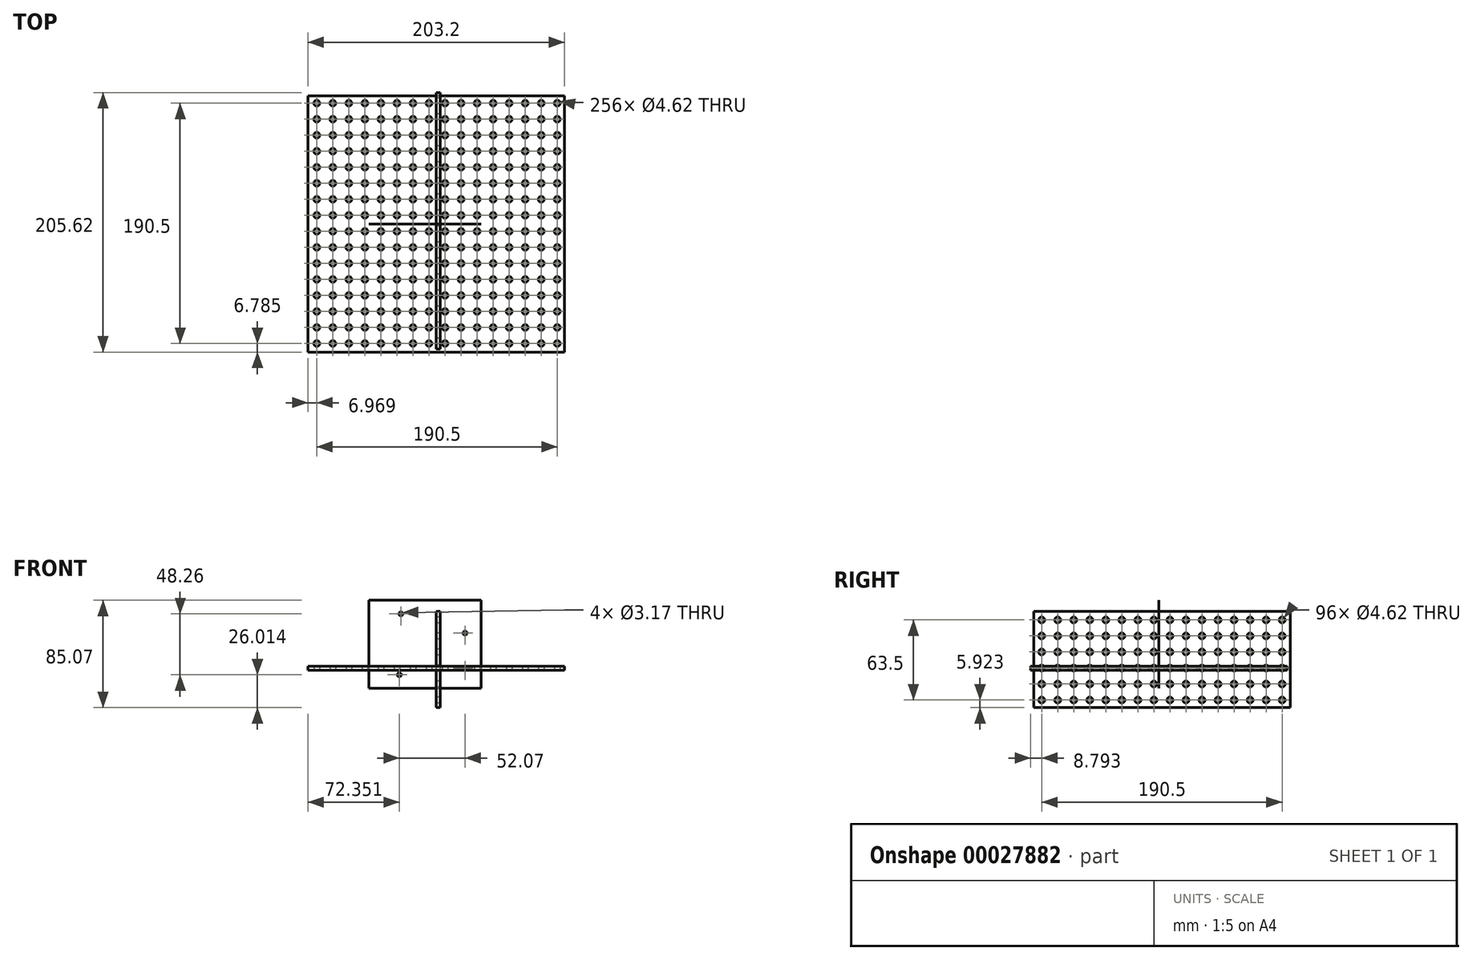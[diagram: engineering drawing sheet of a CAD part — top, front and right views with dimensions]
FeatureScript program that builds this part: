
annotation { "Feature Type Name" : "Feature", "Feature Type Description" : "" }
export const myFeature = defineFeature(function(context is Context, id is Id, definition is map)
    precondition{}
    {
        {
            var Q0;
            Q0=qCreatedBy(makeId("Top.planeOp"),FACE);
            var sketch = newSketch(context, id + "F0", { "sketchPlane" : qUnion([Q0])});
            skLineSegment(sketch, "E0.rect.bottom", {"start": v(101.6, 101.6) * mm, "end": v(-101.6, 101.6) * mm});
            skLineSegment(sketch, "E0.rect.left", {"start": v(101.6, 101.6) * mm, "end": v(101.6, -101.6) * mm});
            skLineSegment(sketch, "E0.rect.right", {"start": v(-101.6, 101.6) * mm, "end": v(-101.6, -101.6) * mm});
            skPoint(sketch, "E0.rect.middle", {"position": v(0, 0) * mm});
            skCircle(sketch, "E1", {"center": v(-94.63, 95.69) * mm, "radius": 2.31 * mm});
            skCircle(sketch, "E2.0.1.0", {"center": v(-94.63, 82.99) * mm, "radius": 2.31 * mm});
            skCircle(sketch, "E2.0.2.0", {"center": v(-94.63, 70.29) * mm, "radius": 2.31 * mm});
            skCircle(sketch, "E2.0.3.0", {"center": v(-94.63, 57.59) * mm, "radius": 2.31 * mm});
            skCircle(sketch, "E2.0.4.0", {"center": v(-94.63, 44.89) * mm, "radius": 2.31 * mm});
            skCircle(sketch, "E2.0.5.0", {"center": v(-94.63, 32.19) * mm, "radius": 2.31 * mm});
            skCircle(sketch, "E2.0.6.0", {"center": v(-94.63, 19.49) * mm, "radius": 2.31 * mm});
            skCircle(sketch, "E2.0.7.0", {"center": v(-94.63, 6.79) * mm, "radius": 2.31 * mm});
            skCircle(sketch, "E2.0.8.0", {"center": v(-94.63, -5.91) * mm, "radius": 2.31 * mm});
            skCircle(sketch, "E2.0.9.0", {"center": v(-94.63, -18.61) * mm, "radius": 2.31 * mm});
            skCircle(sketch, "E2.1.0.0", {"center": v(-81.93, 95.69) * mm, "radius": 2.31 * mm});
            skCircle(sketch, "E2.1.1.0", {"center": v(-81.93, 82.99) * mm, "radius": 2.31 * mm});
            skCircle(sketch, "E2.1.2.0", {"center": v(-81.93, 70.29) * mm, "radius": 2.31 * mm});
            skCircle(sketch, "E2.1.3.0", {"center": v(-81.93, 57.59) * mm, "radius": 2.31 * mm});
            skCircle(sketch, "E2.1.4.0", {"center": v(-81.93, 44.89) * mm, "radius": 2.31 * mm});
            skCircle(sketch, "E2.1.5.0", {"center": v(-81.93, 32.19) * mm, "radius": 2.31 * mm});
            skCircle(sketch, "E2.1.6.0", {"center": v(-81.93, 19.49) * mm, "radius": 2.31 * mm});
            skCircle(sketch, "E2.1.7.0", {"center": v(-81.93, 6.79) * mm, "radius": 2.31 * mm});
            skCircle(sketch, "E2.1.8.0", {"center": v(-81.93, -5.91) * mm, "radius": 2.31 * mm});
            skCircle(sketch, "E2.1.9.0", {"center": v(-81.93, -18.61) * mm, "radius": 2.31 * mm});
            skCircle(sketch, "E2.2.0.0", {"center": v(-69.23, 95.69) * mm, "radius": 2.31 * mm});
            skCircle(sketch, "E2.2.1.0", {"center": v(-69.23, 82.99) * mm, "radius": 2.31 * mm});
            skCircle(sketch, "E2.2.2.0", {"center": v(-69.23, 70.29) * mm, "radius": 2.31 * mm});
            skCircle(sketch, "E2.2.3.0", {"center": v(-69.23, 57.59) * mm, "radius": 2.31 * mm});
            skCircle(sketch, "E2.2.4.0", {"center": v(-69.23, 44.89) * mm, "radius": 2.31 * mm});
            skCircle(sketch, "E2.2.5.0", {"center": v(-69.23, 32.19) * mm, "radius": 2.31 * mm});
            skCircle(sketch, "E2.2.6.0", {"center": v(-69.23, 19.49) * mm, "radius": 2.31 * mm});
            skCircle(sketch, "E2.2.7.0", {"center": v(-69.23, 6.79) * mm, "radius": 2.31 * mm});
            skCircle(sketch, "E2.2.8.0", {"center": v(-69.23, -5.91) * mm, "radius": 2.31 * mm});
            skCircle(sketch, "E2.2.9.0", {"center": v(-69.23, -18.61) * mm, "radius": 2.31 * mm});
            skCircle(sketch, "E2.3.0.0", {"center": v(-56.53, 95.69) * mm, "radius": 2.31 * mm});
            skCircle(sketch, "E2.3.1.0", {"center": v(-56.53, 82.99) * mm, "radius": 2.31 * mm});
            skCircle(sketch, "E2.3.2.0", {"center": v(-56.53, 70.29) * mm, "radius": 2.31 * mm});
            skCircle(sketch, "E2.3.3.0", {"center": v(-56.53, 57.59) * mm, "radius": 2.31 * mm});
            skCircle(sketch, "E2.3.4.0", {"center": v(-56.53, 44.89) * mm, "radius": 2.31 * mm});
            skCircle(sketch, "E2.3.5.0", {"center": v(-56.53, 32.19) * mm, "radius": 2.31 * mm});
            skCircle(sketch, "E2.3.6.0", {"center": v(-56.53, 19.49) * mm, "radius": 2.31 * mm});
            skCircle(sketch, "E2.3.7.0", {"center": v(-56.53, 6.79) * mm, "radius": 2.31 * mm});
            skCircle(sketch, "E2.3.8.0", {"center": v(-56.53, -5.91) * mm, "radius": 2.31 * mm});
            skCircle(sketch, "E2.3.9.0", {"center": v(-56.53, -18.61) * mm, "radius": 2.31 * mm});
            skCircle(sketch, "E2.4.0.0", {"center": v(-43.83, 95.69) * mm, "radius": 2.31 * mm});
            skCircle(sketch, "E2.4.1.0", {"center": v(-43.83, 82.99) * mm, "radius": 2.31 * mm});
            skCircle(sketch, "E2.4.2.0", {"center": v(-43.83, 70.29) * mm, "radius": 2.31 * mm});
            skCircle(sketch, "E2.4.3.0", {"center": v(-43.83, 57.59) * mm, "radius": 2.31 * mm});
            skCircle(sketch, "E2.4.4.0", {"center": v(-43.83, 44.89) * mm, "radius": 2.31 * mm});
            skCircle(sketch, "E2.4.5.0", {"center": v(-43.83, 32.19) * mm, "radius": 2.31 * mm});
            skCircle(sketch, "E2.4.6.0", {"center": v(-43.83, 19.49) * mm, "radius": 2.31 * mm});
            skCircle(sketch, "E2.4.7.0", {"center": v(-43.83, 6.79) * mm, "radius": 2.31 * mm});
            skCircle(sketch, "E2.4.8.0", {"center": v(-43.83, -5.91) * mm, "radius": 2.31 * mm});
            skCircle(sketch, "E2.4.9.0", {"center": v(-43.83, -18.61) * mm, "radius": 2.31 * mm});
            skCircle(sketch, "E2.5.0.0", {"center": v(-31.13, 95.69) * mm, "radius": 2.31 * mm});
            skCircle(sketch, "E2.5.1.0", {"center": v(-31.13, 82.99) * mm, "radius": 2.31 * mm});
            skCircle(sketch, "E2.5.2.0", {"center": v(-31.13, 70.29) * mm, "radius": 2.31 * mm});
            skCircle(sketch, "E2.5.3.0", {"center": v(-31.13, 57.59) * mm, "radius": 2.31 * mm});
            skCircle(sketch, "E2.5.4.0", {"center": v(-31.13, 44.89) * mm, "radius": 2.31 * mm});
            skCircle(sketch, "E2.5.5.0", {"center": v(-31.13, 32.19) * mm, "radius": 2.31 * mm});
            skCircle(sketch, "E2.5.6.0", {"center": v(-31.13, 19.49) * mm, "radius": 2.31 * mm});
            skCircle(sketch, "E2.5.7.0", {"center": v(-31.13, 6.79) * mm, "radius": 2.31 * mm});
            skCircle(sketch, "E2.5.8.0", {"center": v(-31.13, -5.91) * mm, "radius": 2.31 * mm});
            skCircle(sketch, "E2.5.9.0", {"center": v(-31.13, -18.61) * mm, "radius": 2.31 * mm});
            skCircle(sketch, "E2.6.0.0", {"center": v(-18.43, 95.69) * mm, "radius": 2.31 * mm});
            skCircle(sketch, "E2.6.1.0", {"center": v(-18.43, 82.99) * mm, "radius": 2.31 * mm});
            skCircle(sketch, "E2.6.2.0", {"center": v(-18.43, 70.29) * mm, "radius": 2.31 * mm});
            skCircle(sketch, "E2.6.3.0", {"center": v(-18.43, 57.59) * mm, "radius": 2.31 * mm});
            skCircle(sketch, "E2.6.4.0", {"center": v(-18.43, 44.89) * mm, "radius": 2.31 * mm});
            skCircle(sketch, "E2.6.5.0", {"center": v(-18.43, 32.19) * mm, "radius": 2.31 * mm});
            skCircle(sketch, "E2.6.6.0", {"center": v(-18.43, 19.49) * mm, "radius": 2.31 * mm});
            skCircle(sketch, "E2.6.7.0", {"center": v(-18.43, 6.79) * mm, "radius": 2.31 * mm});
            skCircle(sketch, "E2.6.8.0", {"center": v(-18.43, -5.91) * mm, "radius": 2.31 * mm});
            skCircle(sketch, "E2.6.9.0", {"center": v(-18.43, -18.61) * mm, "radius": 2.31 * mm});
            skCircle(sketch, "E2.7.0.0", {"center": v(-5.73, 95.69) * mm, "radius": 2.31 * mm});
            skCircle(sketch, "E2.7.1.0", {"center": v(-5.73, 82.99) * mm, "radius": 2.31 * mm});
            skCircle(sketch, "E2.7.2.0", {"center": v(-5.73, 70.29) * mm, "radius": 2.31 * mm});
            skCircle(sketch, "E2.7.3.0", {"center": v(-5.73, 57.59) * mm, "radius": 2.31 * mm});
            skCircle(sketch, "E2.7.4.0", {"center": v(-5.73, 44.89) * mm, "radius": 2.31 * mm});
            skCircle(sketch, "E2.7.5.0", {"center": v(-5.73, 32.19) * mm, "radius": 2.31 * mm});
            skCircle(sketch, "E2.7.6.0", {"center": v(-5.73, 19.49) * mm, "radius": 2.31 * mm});
            skCircle(sketch, "E2.7.7.0", {"center": v(-5.73, 6.79) * mm, "radius": 2.31 * mm});
            skCircle(sketch, "E2.7.8.0", {"center": v(-5.73, -5.91) * mm, "radius": 2.31 * mm});
            skCircle(sketch, "E2.7.9.0", {"center": v(-5.73, -18.61) * mm, "radius": 2.31 * mm});
            skCircle(sketch, "E2.8.0.0", {"center": v(6.97, 95.69) * mm, "radius": 2.31 * mm});
            skCircle(sketch, "E2.8.1.0", {"center": v(6.97, 82.99) * mm, "radius": 2.31 * mm});
            skCircle(sketch, "E2.8.2.0", {"center": v(6.97, 70.29) * mm, "radius": 2.31 * mm});
            skCircle(sketch, "E2.8.3.0", {"center": v(6.97, 57.59) * mm, "radius": 2.31 * mm});
            skCircle(sketch, "E2.8.4.0", {"center": v(6.97, 44.89) * mm, "radius": 2.31 * mm});
            skCircle(sketch, "E2.8.5.0", {"center": v(6.97, 32.19) * mm, "radius": 2.31 * mm});
            skCircle(sketch, "E2.8.6.0", {"center": v(6.97, 19.49) * mm, "radius": 2.31 * mm});
            skCircle(sketch, "E2.8.7.0", {"center": v(6.97, 6.79) * mm, "radius": 2.31 * mm});
            skCircle(sketch, "E2.8.8.0", {"center": v(6.97, -5.91) * mm, "radius": 2.31 * mm});
            skCircle(sketch, "E2.8.9.0", {"center": v(6.97, -18.61) * mm, "radius": 2.31 * mm});
            skCircle(sketch, "E2.9.0.0", {"center": v(19.67, 95.69) * mm, "radius": 2.31 * mm});
            skCircle(sketch, "E2.9.1.0", {"center": v(19.67, 82.99) * mm, "radius": 2.31 * mm});
            skCircle(sketch, "E2.9.2.0", {"center": v(19.67, 70.29) * mm, "radius": 2.31 * mm});
            skCircle(sketch, "E2.9.3.0", {"center": v(19.67, 57.59) * mm, "radius": 2.31 * mm});
            skCircle(sketch, "E2.9.4.0", {"center": v(19.67, 44.89) * mm, "radius": 2.31 * mm});
            skCircle(sketch, "E2.9.5.0", {"center": v(19.67, 32.19) * mm, "radius": 2.31 * mm});
            skCircle(sketch, "E2.9.6.0", {"center": v(19.67, 19.49) * mm, "radius": 2.31 * mm});
            skCircle(sketch, "E2.9.7.0", {"center": v(19.67, 6.79) * mm, "radius": 2.31 * mm});
            skCircle(sketch, "E2.9.8.0", {"center": v(19.67, -5.91) * mm, "radius": 2.31 * mm});
            skCircle(sketch, "E2.9.9.0", {"center": v(19.67, -18.61) * mm, "radius": 2.31 * mm});
            skLineSegment(sketch, "E2.direction1", {"start": v(-94.63, 95.69) * mm, "end": v(-81.93, 95.69) * mm, "construction": true});
            skLineSegment(sketch, "E2.direction2", {"start": v(-94.63, 95.69) * mm, "end": v(-94.63, 82.99) * mm, "construction": true});
            skCircle(sketch, "E3.0.0.10", {"center": v(-94.63, -31.31) * mm, "radius": 2.31 * mm});
            skCircle(sketch, "E3.0.0.11", {"center": v(-94.63, -44.01) * mm, "radius": 2.31 * mm});
            skCircle(sketch, "E3.0.0.12", {"center": v(-94.63, -56.71) * mm, "radius": 2.31 * mm});
            skCircle(sketch, "E3.0.0.13", {"center": v(-94.63, -69.41) * mm, "radius": 2.31 * mm});
            skCircle(sketch, "E3.0.0.14", {"center": v(-94.63, -82.11) * mm, "radius": 2.31 * mm});
            skCircle(sketch, "E3.0.0.15", {"center": v(-94.63, -94.81) * mm, "radius": 2.31 * mm});
            skCircle(sketch, "E3.0.1.10", {"center": v(-81.93, -31.31) * mm, "radius": 2.31 * mm});
            skCircle(sketch, "E3.0.1.11", {"center": v(-81.93, -44.01) * mm, "radius": 2.31 * mm});
            skCircle(sketch, "E3.0.1.12", {"center": v(-81.93, -56.71) * mm, "radius": 2.31 * mm});
            skCircle(sketch, "E3.0.1.13", {"center": v(-81.93, -69.41) * mm, "radius": 2.31 * mm});
            skCircle(sketch, "E3.0.1.14", {"center": v(-81.93, -82.11) * mm, "radius": 2.31 * mm});
            skCircle(sketch, "E3.0.1.15", {"center": v(-81.93, -94.81) * mm, "radius": 2.31 * mm});
            skCircle(sketch, "E3.0.2.10", {"center": v(-69.23, -31.31) * mm, "radius": 2.31 * mm});
            skCircle(sketch, "E3.0.2.11", {"center": v(-69.23, -44.01) * mm, "radius": 2.31 * mm});
            skCircle(sketch, "E3.0.2.12", {"center": v(-69.23, -56.71) * mm, "radius": 2.31 * mm});
            skCircle(sketch, "E3.0.2.13", {"center": v(-69.23, -69.41) * mm, "radius": 2.31 * mm});
            skCircle(sketch, "E3.0.2.14", {"center": v(-69.23, -82.11) * mm, "radius": 2.31 * mm});
            skCircle(sketch, "E3.0.2.15", {"center": v(-69.23, -94.81) * mm, "radius": 2.31 * mm});
            skCircle(sketch, "E3.0.3.10", {"center": v(-56.53, -31.31) * mm, "radius": 2.31 * mm});
            skCircle(sketch, "E3.0.3.11", {"center": v(-56.53, -44.01) * mm, "radius": 2.31 * mm});
            skCircle(sketch, "E3.0.3.12", {"center": v(-56.53, -56.71) * mm, "radius": 2.31 * mm});
            skCircle(sketch, "E3.0.3.13", {"center": v(-56.53, -69.41) * mm, "radius": 2.31 * mm});
            skCircle(sketch, "E3.0.3.14", {"center": v(-56.53, -82.11) * mm, "radius": 2.31 * mm});
            skCircle(sketch, "E3.0.3.15", {"center": v(-56.53, -94.81) * mm, "radius": 2.31 * mm});
            skCircle(sketch, "E3.0.4.10", {"center": v(-43.83, -31.31) * mm, "radius": 2.31 * mm});
            skCircle(sketch, "E3.0.4.11", {"center": v(-43.83, -44.01) * mm, "radius": 2.31 * mm});
            skCircle(sketch, "E3.0.4.12", {"center": v(-43.83, -56.71) * mm, "radius": 2.31 * mm});
            skCircle(sketch, "E3.0.4.13", {"center": v(-43.83, -69.41) * mm, "radius": 2.31 * mm});
            skCircle(sketch, "E3.0.4.14", {"center": v(-43.83, -82.11) * mm, "radius": 2.31 * mm});
            skCircle(sketch, "E3.0.4.15", {"center": v(-43.83, -94.81) * mm, "radius": 2.31 * mm});
            skCircle(sketch, "E3.0.5.10", {"center": v(-31.13, -31.31) * mm, "radius": 2.31 * mm});
            skCircle(sketch, "E3.0.5.11", {"center": v(-31.13, -44.01) * mm, "radius": 2.31 * mm});
            skCircle(sketch, "E3.0.5.12", {"center": v(-31.13, -56.71) * mm, "radius": 2.31 * mm});
            skCircle(sketch, "E3.0.5.13", {"center": v(-31.13, -69.41) * mm, "radius": 2.31 * mm});
            skCircle(sketch, "E3.0.5.14", {"center": v(-31.13, -82.11) * mm, "radius": 2.31 * mm});
            skCircle(sketch, "E3.0.5.15", {"center": v(-31.13, -94.81) * mm, "radius": 2.31 * mm});
            skCircle(sketch, "E3.0.6.10", {"center": v(-18.43, -31.31) * mm, "radius": 2.31 * mm});
            skCircle(sketch, "E3.0.6.11", {"center": v(-18.43, -44.01) * mm, "radius": 2.31 * mm});
            skCircle(sketch, "E3.0.6.12", {"center": v(-18.43, -56.71) * mm, "radius": 2.31 * mm});
            skCircle(sketch, "E3.0.6.13", {"center": v(-18.43, -69.41) * mm, "radius": 2.31 * mm});
            skCircle(sketch, "E3.0.6.14", {"center": v(-18.43, -82.11) * mm, "radius": 2.31 * mm});
            skCircle(sketch, "E3.0.6.15", {"center": v(-18.43, -94.81) * mm, "radius": 2.31 * mm});
            skCircle(sketch, "E3.0.7.10", {"center": v(-5.73, -31.31) * mm, "radius": 2.31 * mm});
            skCircle(sketch, "E3.0.7.11", {"center": v(-5.73, -44.01) * mm, "radius": 2.31 * mm});
            skCircle(sketch, "E3.0.7.12", {"center": v(-5.73, -56.71) * mm, "radius": 2.31 * mm});
            skCircle(sketch, "E3.0.7.13", {"center": v(-5.73, -69.41) * mm, "radius": 2.31 * mm});
            skCircle(sketch, "E3.0.7.14", {"center": v(-5.73, -82.11) * mm, "radius": 2.31 * mm});
            skCircle(sketch, "E3.0.7.15", {"center": v(-5.73, -94.81) * mm, "radius": 2.31 * mm});
            skCircle(sketch, "E3.0.8.10", {"center": v(6.97, -31.31) * mm, "radius": 2.31 * mm});
            skCircle(sketch, "E3.0.8.11", {"center": v(6.97, -44.01) * mm, "radius": 2.31 * mm});
            skCircle(sketch, "E3.0.8.12", {"center": v(6.97, -56.71) * mm, "radius": 2.31 * mm});
            skCircle(sketch, "E3.0.8.13", {"center": v(6.97, -69.41) * mm, "radius": 2.31 * mm});
            skCircle(sketch, "E3.0.8.14", {"center": v(6.97, -82.11) * mm, "radius": 2.31 * mm});
            skCircle(sketch, "E3.0.8.15", {"center": v(6.97, -94.81) * mm, "radius": 2.31 * mm});
            skCircle(sketch, "E3.0.9.10", {"center": v(19.67, -31.31) * mm, "radius": 2.31 * mm});
            skCircle(sketch, "E3.0.9.11", {"center": v(19.67, -44.01) * mm, "radius": 2.31 * mm});
            skCircle(sketch, "E3.0.9.12", {"center": v(19.67, -56.71) * mm, "radius": 2.31 * mm});
            skCircle(sketch, "E3.0.9.13", {"center": v(19.67, -69.41) * mm, "radius": 2.31 * mm});
            skCircle(sketch, "E3.0.9.14", {"center": v(19.67, -82.11) * mm, "radius": 2.31 * mm});
            skCircle(sketch, "E3.0.9.15", {"center": v(19.67, -94.81) * mm, "radius": 2.31 * mm});
            skCircle(sketch, "E4.0.10.0", {"center": v(32.37, 95.69) * mm, "radius": 2.31 * mm});
            skCircle(sketch, "E4.0.10.1", {"center": v(32.37, 82.99) * mm, "radius": 2.31 * mm});
            skCircle(sketch, "E4.0.10.2", {"center": v(32.37, 70.29) * mm, "radius": 2.31 * mm});
            skCircle(sketch, "E4.0.10.3", {"center": v(32.37, 57.59) * mm, "radius": 2.31 * mm});
            skCircle(sketch, "E4.0.10.4", {"center": v(32.37, 44.89) * mm, "radius": 2.31 * mm});
            skCircle(sketch, "E4.0.10.5", {"center": v(32.37, 32.19) * mm, "radius": 2.31 * mm});
            skCircle(sketch, "E4.0.10.6", {"center": v(32.37, 19.49) * mm, "radius": 2.31 * mm});
            skCircle(sketch, "E4.0.10.7", {"center": v(32.37, 6.79) * mm, "radius": 2.31 * mm});
            skCircle(sketch, "E4.0.10.8", {"center": v(32.37, -5.91) * mm, "radius": 2.31 * mm});
            skCircle(sketch, "E4.0.10.9", {"center": v(32.37, -18.61) * mm, "radius": 2.31 * mm});
            skCircle(sketch, "E4.0.10.10", {"center": v(32.37, -31.31) * mm, "radius": 2.31 * mm});
            skCircle(sketch, "E4.0.10.11", {"center": v(32.37, -44.01) * mm, "radius": 2.31 * mm});
            skCircle(sketch, "E4.0.10.12", {"center": v(32.37, -56.71) * mm, "radius": 2.31 * mm});
            skCircle(sketch, "E4.0.10.13", {"center": v(32.37, -69.41) * mm, "radius": 2.31 * mm});
            skCircle(sketch, "E4.0.10.14", {"center": v(32.37, -82.11) * mm, "radius": 2.31 * mm});
            skCircle(sketch, "E4.0.10.15", {"center": v(32.37, -94.81) * mm, "radius": 2.31 * mm});
            skCircle(sketch, "E4.0.11.0", {"center": v(45.07, 95.69) * mm, "radius": 2.31 * mm});
            skCircle(sketch, "E4.0.11.1", {"center": v(45.07, 82.99) * mm, "radius": 2.31 * mm});
            skCircle(sketch, "E4.0.11.2", {"center": v(45.07, 70.29) * mm, "radius": 2.31 * mm});
            skCircle(sketch, "E4.0.11.3", {"center": v(45.07, 57.59) * mm, "radius": 2.31 * mm});
            skCircle(sketch, "E4.0.11.4", {"center": v(45.07, 44.89) * mm, "radius": 2.31 * mm});
            skCircle(sketch, "E4.0.11.5", {"center": v(45.07, 32.19) * mm, "radius": 2.31 * mm});
            skCircle(sketch, "E4.0.11.6", {"center": v(45.07, 19.49) * mm, "radius": 2.31 * mm});
            skCircle(sketch, "E4.0.11.7", {"center": v(45.07, 6.79) * mm, "radius": 2.31 * mm});
            skCircle(sketch, "E4.0.11.8", {"center": v(45.07, -5.91) * mm, "radius": 2.31 * mm});
            skCircle(sketch, "E4.0.11.9", {"center": v(45.07, -18.61) * mm, "radius": 2.31 * mm});
            skCircle(sketch, "E4.0.11.10", {"center": v(45.07, -31.31) * mm, "radius": 2.31 * mm});
            skCircle(sketch, "E4.0.11.11", {"center": v(45.07, -44.01) * mm, "radius": 2.31 * mm});
            skCircle(sketch, "E4.0.11.12", {"center": v(45.07, -56.71) * mm, "radius": 2.31 * mm});
            skCircle(sketch, "E4.0.11.13", {"center": v(45.07, -69.41) * mm, "radius": 2.31 * mm});
            skCircle(sketch, "E4.0.11.14", {"center": v(45.07, -82.11) * mm, "radius": 2.31 * mm});
            skCircle(sketch, "E4.0.11.15", {"center": v(45.07, -94.81) * mm, "radius": 2.31 * mm});
            skCircle(sketch, "E4.0.12.0", {"center": v(57.77, 95.69) * mm, "radius": 2.31 * mm});
            skCircle(sketch, "E4.0.12.1", {"center": v(57.77, 82.99) * mm, "radius": 2.31 * mm});
            skCircle(sketch, "E4.0.12.2", {"center": v(57.77, 70.29) * mm, "radius": 2.31 * mm});
            skCircle(sketch, "E4.0.12.3", {"center": v(57.77, 57.59) * mm, "radius": 2.31 * mm});
            skCircle(sketch, "E4.0.12.4", {"center": v(57.77, 44.89) * mm, "radius": 2.31 * mm});
            skCircle(sketch, "E4.0.12.5", {"center": v(57.77, 32.19) * mm, "radius": 2.31 * mm});
            skCircle(sketch, "E4.0.12.6", {"center": v(57.77, 19.49) * mm, "radius": 2.31 * mm});
            skCircle(sketch, "E4.0.12.7", {"center": v(57.77, 6.79) * mm, "radius": 2.31 * mm});
            skCircle(sketch, "E4.0.12.8", {"center": v(57.77, -5.91) * mm, "radius": 2.31 * mm});
            skCircle(sketch, "E4.0.12.9", {"center": v(57.77, -18.61) * mm, "radius": 2.31 * mm});
            skCircle(sketch, "E4.0.12.10", {"center": v(57.77, -31.31) * mm, "radius": 2.31 * mm});
            skCircle(sketch, "E4.0.12.11", {"center": v(57.77, -44.01) * mm, "radius": 2.31 * mm});
            skCircle(sketch, "E4.0.12.12", {"center": v(57.77, -56.71) * mm, "radius": 2.31 * mm});
            skCircle(sketch, "E4.0.12.13", {"center": v(57.77, -69.41) * mm, "radius": 2.31 * mm});
            skCircle(sketch, "E4.0.12.14", {"center": v(57.77, -82.11) * mm, "radius": 2.31 * mm});
            skCircle(sketch, "E4.0.12.15", {"center": v(57.77, -94.81) * mm, "radius": 2.31 * mm});
            skCircle(sketch, "E4.0.13.0", {"center": v(70.47, 95.69) * mm, "radius": 2.31 * mm});
            skCircle(sketch, "E4.0.13.1", {"center": v(70.47, 82.99) * mm, "radius": 2.31 * mm});
            skCircle(sketch, "E4.0.13.2", {"center": v(70.47, 70.29) * mm, "radius": 2.31 * mm});
            skCircle(sketch, "E4.0.13.3", {"center": v(70.47, 57.59) * mm, "radius": 2.31 * mm});
            skCircle(sketch, "E4.0.13.4", {"center": v(70.47, 44.89) * mm, "radius": 2.31 * mm});
            skCircle(sketch, "E4.0.13.5", {"center": v(70.47, 32.19) * mm, "radius": 2.31 * mm});
            skCircle(sketch, "E4.0.13.6", {"center": v(70.47, 19.49) * mm, "radius": 2.31 * mm});
            skCircle(sketch, "E4.0.13.7", {"center": v(70.47, 6.79) * mm, "radius": 2.31 * mm});
            skCircle(sketch, "E4.0.13.8", {"center": v(70.47, -5.91) * mm, "radius": 2.31 * mm});
            skCircle(sketch, "E4.0.13.9", {"center": v(70.47, -18.61) * mm, "radius": 2.31 * mm});
            skCircle(sketch, "E4.0.13.10", {"center": v(70.47, -31.31) * mm, "radius": 2.31 * mm});
            skCircle(sketch, "E4.0.13.11", {"center": v(70.47, -44.01) * mm, "radius": 2.31 * mm});
            skCircle(sketch, "E4.0.13.12", {"center": v(70.47, -56.71) * mm, "radius": 2.31 * mm});
            skCircle(sketch, "E4.0.13.13", {"center": v(70.47, -69.41) * mm, "radius": 2.31 * mm});
            skCircle(sketch, "E4.0.13.14", {"center": v(70.47, -82.11) * mm, "radius": 2.31 * mm});
            skCircle(sketch, "E4.0.13.15", {"center": v(70.47, -94.81) * mm, "radius": 2.31 * mm});
            skCircle(sketch, "E4.0.14.0", {"center": v(83.17, 95.69) * mm, "radius": 2.31 * mm});
            skCircle(sketch, "E4.0.14.1", {"center": v(83.17, 82.99) * mm, "radius": 2.31 * mm});
            skCircle(sketch, "E4.0.14.2", {"center": v(83.17, 70.29) * mm, "radius": 2.31 * mm});
            skCircle(sketch, "E4.0.14.3", {"center": v(83.17, 57.59) * mm, "radius": 2.31 * mm});
            skCircle(sketch, "E4.0.14.4", {"center": v(83.17, 44.89) * mm, "radius": 2.31 * mm});
            skCircle(sketch, "E4.0.14.5", {"center": v(83.17, 32.19) * mm, "radius": 2.31 * mm});
            skCircle(sketch, "E4.0.14.6", {"center": v(83.17, 19.49) * mm, "radius": 2.31 * mm});
            skCircle(sketch, "E4.0.14.7", {"center": v(83.17, 6.79) * mm, "radius": 2.31 * mm});
            skCircle(sketch, "E4.0.14.8", {"center": v(83.17, -5.91) * mm, "radius": 2.31 * mm});
            skCircle(sketch, "E4.0.14.9", {"center": v(83.17, -18.61) * mm, "radius": 2.31 * mm});
            skCircle(sketch, "E4.0.14.10", {"center": v(83.17, -31.31) * mm, "radius": 2.31 * mm});
            skCircle(sketch, "E4.0.14.11", {"center": v(83.17, -44.01) * mm, "radius": 2.31 * mm});
            skCircle(sketch, "E4.0.14.12", {"center": v(83.17, -56.71) * mm, "radius": 2.31 * mm});
            skCircle(sketch, "E4.0.14.13", {"center": v(83.17, -69.41) * mm, "radius": 2.31 * mm});
            skCircle(sketch, "E4.0.14.14", {"center": v(83.17, -82.11) * mm, "radius": 2.31 * mm});
            skCircle(sketch, "E4.0.14.15", {"center": v(83.17, -94.81) * mm, "radius": 2.31 * mm});
            skCircle(sketch, "E4.0.15.0", {"center": v(95.87, 95.69) * mm, "radius": 2.31 * mm});
            skCircle(sketch, "E4.0.15.1", {"center": v(95.87, 82.99) * mm, "radius": 2.31 * mm});
            skCircle(sketch, "E4.0.15.2", {"center": v(95.87, 70.29) * mm, "radius": 2.31 * mm});
            skCircle(sketch, "E4.0.15.3", {"center": v(95.87, 57.59) * mm, "radius": 2.31 * mm});
            skCircle(sketch, "E4.0.15.4", {"center": v(95.87, 44.89) * mm, "radius": 2.31 * mm});
            skCircle(sketch, "E4.0.15.5", {"center": v(95.87, 32.19) * mm, "radius": 2.31 * mm});
            skCircle(sketch, "E4.0.15.6", {"center": v(95.87, 19.49) * mm, "radius": 2.31 * mm});
            skCircle(sketch, "E4.0.15.7", {"center": v(95.87, 6.79) * mm, "radius": 2.31 * mm});
            skCircle(sketch, "E4.0.15.8", {"center": v(95.87, -5.91) * mm, "radius": 2.31 * mm});
            skCircle(sketch, "E4.0.15.9", {"center": v(95.87, -18.61) * mm, "radius": 2.31 * mm});
            skCircle(sketch, "E4.0.15.10", {"center": v(95.87, -31.31) * mm, "radius": 2.31 * mm});
            skCircle(sketch, "E4.0.15.11", {"center": v(95.87, -44.01) * mm, "radius": 2.31 * mm});
            skCircle(sketch, "E4.0.15.12", {"center": v(95.87, -56.71) * mm, "radius": 2.31 * mm});
            skCircle(sketch, "E4.0.15.13", {"center": v(95.87, -69.41) * mm, "radius": 2.31 * mm});
            skCircle(sketch, "E4.0.15.14", {"center": v(95.87, -82.11) * mm, "radius": 2.31 * mm});
            skCircle(sketch, "E4.0.15.15", {"center": v(95.87, -94.81) * mm, "radius": 2.31 * mm});
            skLineSegment(sketch, "E5", {"start": v(-101.6, -101.6) * mm, "end": v(101.6, -101.6) * mm});
            skSolve(sketch);
        }
        {
            var Q0;
            Q0 = qSketchRegion(id + "F0", true);
            var Q1;
            Q1=makeQuery(id+"F0.imprint","IMPRINT",FACE,{"disambiguationData":[TD([[makeQuery(id+"F0.imprint","IMPRINT",EDGE,{"derivedFrom":sQuery(id+"F0.wireOp",EDGE,"E0.rect.bottom")}),1.0]])]});
            extrude(context, id + "F1", {"entities" : qUnion([Q0, Q1]), "depth" : 3.17 * mm});
        }
        {
            var Q0;
            Q0=qCreatedBy(makeId("Front.planeOp"),FACE);
            var sketch = newSketch(context, id + "F2", { "sketchPlane" : qUnion([Q0])});
            skLineSegment(sketch, "E6.bottom", {"start": v(-53.38, 55.62) * mm, "end": v(35.52, 55.62) * mm});
            skLineSegment(sketch, "E6.top", {"start": v(-53.38, -14.23) * mm, "end": v(35.52, -14.23) * mm});
            skLineSegment(sketch, "E6.left", {"start": v(-53.38, 55.62) * mm, "end": v(-53.38, -14.23) * mm});
            skLineSegment(sketch, "E6.right", {"start": v(35.52, 55.62) * mm, "end": v(35.52, -14.23) * mm});
            skCircle(sketch, "E7", {"center": v(-27.98, 44.82) * mm, "radius": 1.59 * mm});
            skCircle(sketch, "E8", {"center": v(-29.25, -3.44) * mm, "radius": 1.59 * mm});
            skCircle(sketch, "E9", {"center": v(22.82, 1.64) * mm, "radius": 1.59 * mm});
            skCircle(sketch, "E10", {"center": v(22.82, 29.58) * mm, "radius": 1.59 * mm});
            skSolve(sketch);
        }
        {
            var Q0;
            Q0 = qSketchRegion(id + "F2", true);
            extrude(context, id + "F3", {"entities" : qUnion([Q0]), "depth" : 1 / 203.2 * mm});
        }
        {
            var Q0;
            Q0=qCreatedBy(makeId("Right.planeOp"),FACE);
            var sketch = newSketch(context, id + "F4", { "sketchPlane" : qUnion([Q0])});
            skLineSegment(sketch, "E11.bottom", {"start": v(-99.18, 46.75) * mm, "end": v(104.02, 46.75) * mm});
            skLineSegment(sketch, "E11.top", {"start": v(-99.18, -29.45) * mm, "end": v(104.02, -29.45) * mm});
            skLineSegment(sketch, "E11.left", {"start": v(-99.18, 46.75) * mm, "end": v(-99.18, -29.45) * mm});
            skLineSegment(sketch, "E11.right", {"start": v(104.02, 46.75) * mm, "end": v(104.02, -29.45) * mm});
            skCircle(sketch, "E12", {"center": v(-92.8, 39.97) * mm, "radius": 2.31 * mm});
            skCircle(sketch, "E13.0.1.0", {"center": v(-92.8, 27.27) * mm, "radius": 2.31 * mm});
            skCircle(sketch, "E13.0.2.0", {"center": v(-92.8, 14.57) * mm, "radius": 2.31 * mm});
            skCircle(sketch, "E13.0.3.0", {"center": v(-92.8, 1.87) * mm, "radius": 2.31 * mm});
            skCircle(sketch, "E13.0.4.0", {"center": v(-92.8, -10.83) * mm, "radius": 2.31 * mm});
            skCircle(sketch, "E13.0.5.0", {"center": v(-92.8, -23.53) * mm, "radius": 2.31 * mm});
            skCircle(sketch, "E13.1.0.0", {"center": v(-80.1, 39.97) * mm, "radius": 2.31 * mm});
            skCircle(sketch, "E13.1.1.0", {"center": v(-80.1, 27.27) * mm, "radius": 2.31 * mm});
            skCircle(sketch, "E13.1.2.0", {"center": v(-80.1, 14.57) * mm, "radius": 2.31 * mm});
            skCircle(sketch, "E13.1.3.0", {"center": v(-80.1, 1.87) * mm, "radius": 2.31 * mm});
            skCircle(sketch, "E13.1.4.0", {"center": v(-80.1, -10.83) * mm, "radius": 2.31 * mm});
            skCircle(sketch, "E13.1.5.0", {"center": v(-80.1, -23.53) * mm, "radius": 2.31 * mm});
            skCircle(sketch, "E13.2.0.0", {"center": v(-67.4, 39.97) * mm, "radius": 2.31 * mm});
            skCircle(sketch, "E13.2.1.0", {"center": v(-67.4, 27.27) * mm, "radius": 2.31 * mm});
            skCircle(sketch, "E13.2.2.0", {"center": v(-67.4, 14.57) * mm, "radius": 2.31 * mm});
            skCircle(sketch, "E13.2.3.0", {"center": v(-67.4, 1.87) * mm, "radius": 2.31 * mm});
            skCircle(sketch, "E13.2.4.0", {"center": v(-67.4, -10.83) * mm, "radius": 2.31 * mm});
            skCircle(sketch, "E13.2.5.0", {"center": v(-67.4, -23.53) * mm, "radius": 2.31 * mm});
            skCircle(sketch, "E13.3.0.0", {"center": v(-54.7, 39.97) * mm, "radius": 2.31 * mm});
            skCircle(sketch, "E13.3.1.0", {"center": v(-54.7, 27.27) * mm, "radius": 2.31 * mm});
            skCircle(sketch, "E13.3.2.0", {"center": v(-54.7, 14.57) * mm, "radius": 2.31 * mm});
            skCircle(sketch, "E13.3.3.0", {"center": v(-54.7, 1.87) * mm, "radius": 2.31 * mm});
            skCircle(sketch, "E13.3.4.0", {"center": v(-54.7, -10.83) * mm, "radius": 2.31 * mm});
            skCircle(sketch, "E13.3.5.0", {"center": v(-54.7, -23.53) * mm, "radius": 2.31 * mm});
            skCircle(sketch, "E13.4.0.0", {"center": v(-42, 39.97) * mm, "radius": 2.31 * mm});
            skCircle(sketch, "E13.4.1.0", {"center": v(-42, 27.27) * mm, "radius": 2.31 * mm});
            skCircle(sketch, "E13.4.2.0", {"center": v(-42, 14.57) * mm, "radius": 2.31 * mm});
            skCircle(sketch, "E13.4.3.0", {"center": v(-42, 1.87) * mm, "radius": 2.31 * mm});
            skCircle(sketch, "E13.4.4.0", {"center": v(-42, -10.83) * mm, "radius": 2.31 * mm});
            skCircle(sketch, "E13.4.5.0", {"center": v(-42, -23.53) * mm, "radius": 2.31 * mm});
            skCircle(sketch, "E13.5.0.0", {"center": v(-29.3, 39.97) * mm, "radius": 2.31 * mm});
            skCircle(sketch, "E13.5.1.0", {"center": v(-29.3, 27.27) * mm, "radius": 2.31 * mm});
            skCircle(sketch, "E13.5.2.0", {"center": v(-29.3, 14.57) * mm, "radius": 2.31 * mm});
            skCircle(sketch, "E13.5.3.0", {"center": v(-29.3, 1.87) * mm, "radius": 2.31 * mm});
            skCircle(sketch, "E13.5.4.0", {"center": v(-29.3, -10.83) * mm, "radius": 2.31 * mm});
            skCircle(sketch, "E13.5.5.0", {"center": v(-29.3, -23.53) * mm, "radius": 2.31 * mm});
            skCircle(sketch, "E13.6.0.0", {"center": v(-16.6, 39.97) * mm, "radius": 2.31 * mm});
            skCircle(sketch, "E13.6.1.0", {"center": v(-16.6, 27.27) * mm, "radius": 2.31 * mm});
            skCircle(sketch, "E13.6.2.0", {"center": v(-16.6, 14.57) * mm, "radius": 2.31 * mm});
            skCircle(sketch, "E13.6.3.0", {"center": v(-16.6, 1.87) * mm, "radius": 2.31 * mm});
            skCircle(sketch, "E13.6.4.0", {"center": v(-16.6, -10.83) * mm, "radius": 2.31 * mm});
            skCircle(sketch, "E13.6.5.0", {"center": v(-16.6, -23.53) * mm, "radius": 2.31 * mm});
            skCircle(sketch, "E13.7.0.0", {"center": v(-3.9, 39.97) * mm, "radius": 2.31 * mm});
            skCircle(sketch, "E13.7.1.0", {"center": v(-3.9, 27.27) * mm, "radius": 2.31 * mm});
            skCircle(sketch, "E13.7.2.0", {"center": v(-3.9, 14.57) * mm, "radius": 2.31 * mm});
            skCircle(sketch, "E13.7.3.0", {"center": v(-3.9, 1.87) * mm, "radius": 2.31 * mm});
            skCircle(sketch, "E13.7.4.0", {"center": v(-3.9, -10.83) * mm, "radius": 2.31 * mm});
            skCircle(sketch, "E13.7.5.0", {"center": v(-3.9, -23.53) * mm, "radius": 2.31 * mm});
            skCircle(sketch, "E13.8.0.0", {"center": v(8.8, 39.97) * mm, "radius": 2.31 * mm});
            skCircle(sketch, "E13.8.1.0", {"center": v(8.8, 27.27) * mm, "radius": 2.31 * mm});
            skCircle(sketch, "E13.8.2.0", {"center": v(8.8, 14.57) * mm, "radius": 2.31 * mm});
            skCircle(sketch, "E13.8.3.0", {"center": v(8.8, 1.87) * mm, "radius": 2.31 * mm});
            skCircle(sketch, "E13.8.4.0", {"center": v(8.8, -10.83) * mm, "radius": 2.31 * mm});
            skCircle(sketch, "E13.8.5.0", {"center": v(8.8, -23.53) * mm, "radius": 2.31 * mm});
            skCircle(sketch, "E13.9.0.0", {"center": v(21.5, 39.97) * mm, "radius": 2.31 * mm});
            skCircle(sketch, "E13.9.1.0", {"center": v(21.5, 27.27) * mm, "radius": 2.31 * mm});
            skCircle(sketch, "E13.9.2.0", {"center": v(21.5, 14.57) * mm, "radius": 2.31 * mm});
            skCircle(sketch, "E13.9.3.0", {"center": v(21.5, 1.87) * mm, "radius": 2.31 * mm});
            skCircle(sketch, "E13.9.4.0", {"center": v(21.5, -10.83) * mm, "radius": 2.31 * mm});
            skCircle(sketch, "E13.9.5.0", {"center": v(21.5, -23.53) * mm, "radius": 2.31 * mm});
            skCircle(sketch, "E13.10.0.0", {"center": v(34.2, 39.97) * mm, "radius": 2.31 * mm});
            skCircle(sketch, "E13.10.1.0", {"center": v(34.2, 27.27) * mm, "radius": 2.31 * mm});
            skCircle(sketch, "E13.10.2.0", {"center": v(34.2, 14.57) * mm, "radius": 2.31 * mm});
            skCircle(sketch, "E13.10.3.0", {"center": v(34.2, 1.87) * mm, "radius": 2.31 * mm});
            skCircle(sketch, "E13.10.4.0", {"center": v(34.2, -10.83) * mm, "radius": 2.31 * mm});
            skCircle(sketch, "E13.10.5.0", {"center": v(34.2, -23.53) * mm, "radius": 2.31 * mm});
            skCircle(sketch, "E13.11.0.0", {"center": v(46.9, 39.97) * mm, "radius": 2.31 * mm});
            skCircle(sketch, "E13.11.1.0", {"center": v(46.9, 27.27) * mm, "radius": 2.31 * mm});
            skCircle(sketch, "E13.11.2.0", {"center": v(46.9, 14.57) * mm, "radius": 2.31 * mm});
            skCircle(sketch, "E13.11.3.0", {"center": v(46.9, 1.87) * mm, "radius": 2.31 * mm});
            skCircle(sketch, "E13.11.4.0", {"center": v(46.9, -10.83) * mm, "radius": 2.31 * mm});
            skCircle(sketch, "E13.11.5.0", {"center": v(46.9, -23.53) * mm, "radius": 2.31 * mm});
            skCircle(sketch, "E13.12.0.0", {"center": v(59.6, 39.97) * mm, "radius": 2.31 * mm});
            skCircle(sketch, "E13.12.1.0", {"center": v(59.6, 27.27) * mm, "radius": 2.31 * mm});
            skCircle(sketch, "E13.12.2.0", {"center": v(59.6, 14.57) * mm, "radius": 2.31 * mm});
            skCircle(sketch, "E13.12.3.0", {"center": v(59.6, 1.87) * mm, "radius": 2.31 * mm});
            skCircle(sketch, "E13.12.4.0", {"center": v(59.6, -10.83) * mm, "radius": 2.31 * mm});
            skCircle(sketch, "E13.12.5.0", {"center": v(59.6, -23.53) * mm, "radius": 2.31 * mm});
            skCircle(sketch, "E13.13.0.0", {"center": v(72.3, 39.97) * mm, "radius": 2.31 * mm});
            skCircle(sketch, "E13.13.1.0", {"center": v(72.3, 27.27) * mm, "radius": 2.31 * mm});
            skCircle(sketch, "E13.13.2.0", {"center": v(72.3, 14.57) * mm, "radius": 2.31 * mm});
            skCircle(sketch, "E13.13.3.0", {"center": v(72.3, 1.87) * mm, "radius": 2.31 * mm});
            skCircle(sketch, "E13.13.4.0", {"center": v(72.3, -10.83) * mm, "radius": 2.31 * mm});
            skCircle(sketch, "E13.13.5.0", {"center": v(72.3, -23.53) * mm, "radius": 2.31 * mm});
            skCircle(sketch, "E13.14.0.0", {"center": v(85, 39.97) * mm, "radius": 2.31 * mm});
            skCircle(sketch, "E13.14.1.0", {"center": v(85, 27.27) * mm, "radius": 2.31 * mm});
            skCircle(sketch, "E13.14.2.0", {"center": v(85, 14.57) * mm, "radius": 2.31 * mm});
            skCircle(sketch, "E13.14.3.0", {"center": v(85, 1.87) * mm, "radius": 2.31 * mm});
            skCircle(sketch, "E13.14.4.0", {"center": v(85, -10.83) * mm, "radius": 2.31 * mm});
            skCircle(sketch, "E13.14.5.0", {"center": v(85, -23.53) * mm, "radius": 2.31 * mm});
            skCircle(sketch, "E13.15.0.0", {"center": v(97.7, 39.97) * mm, "radius": 2.31 * mm});
            skCircle(sketch, "E13.15.1.0", {"center": v(97.7, 27.27) * mm, "radius": 2.31 * mm});
            skCircle(sketch, "E13.15.2.0", {"center": v(97.7, 14.57) * mm, "radius": 2.31 * mm});
            skCircle(sketch, "E13.15.3.0", {"center": v(97.7, 1.87) * mm, "radius": 2.31 * mm});
            skCircle(sketch, "E13.15.4.0", {"center": v(97.7, -10.83) * mm, "radius": 2.31 * mm});
            skCircle(sketch, "E13.15.5.0", {"center": v(97.7, -23.53) * mm, "radius": 2.31 * mm});
            skLineSegment(sketch, "E13.direction1", {"start": v(-92.8, 39.97) * mm, "end": v(-80.1, 39.97) * mm, "construction": true});
            skLineSegment(sketch, "E13.direction2", {"start": v(-92.8, 39.97) * mm, "end": v(-92.8, 27.27) * mm, "construction": true});
            skSolve(sketch);
        }
        {
            var Q0;
            Q0=makeQuery(id+"F4.imprint","IMPRINT",FACE,{"disambiguationData":[TD([[makeQuery(id+"F4.imprint","IMPRINT",EDGE,{"derivedFrom":sQuery(id+"F4.wireOp",EDGE,"E11.bottom")}),-1.0]])]});
            extrude(context, id + "F5", {"entities" : qUnion([Q0]), "depth" : 3.17 * mm});
        }
    });
